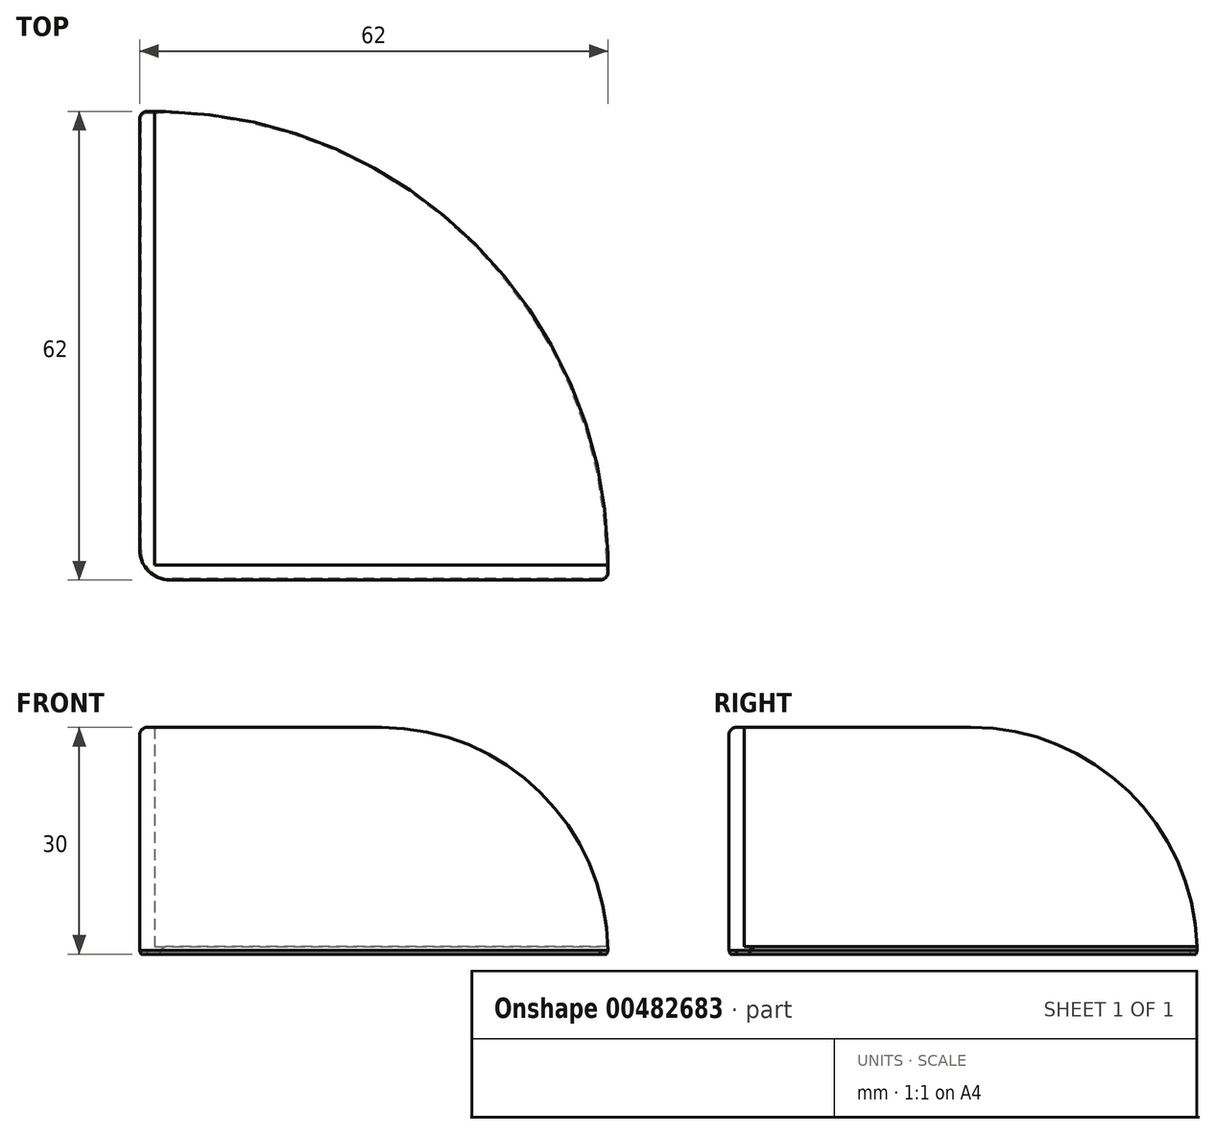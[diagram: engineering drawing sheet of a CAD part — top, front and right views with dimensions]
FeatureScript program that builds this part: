
annotation { "Feature Type Name" : "Feature", "Feature Type Description" : "" }
export const myFeature = defineFeature(function(context is Context, id is Id, definition is map)
    precondition{}
    {
        {
            var Q0;
            Q0=qCreatedBy(makeId("Top.planeOp"),FACE);
            var sketch = newSketch(context, id + "F0", { "sketchPlane" : qUnion([Q0])});
            skLineSegment(sketch, "E0.bottom", {"start": v(0, 0) * mm, "end": v(60, 0) * mm});
            skLineSegment(sketch, "E0.top", {"start": v(0, 60) * mm, "end": v(60, 60) * mm, "construction": true});
            skLineSegment(sketch, "E0.left", {"start": v(0, 0) * mm, "end": v(0, 60) * mm});
            skLineSegment(sketch, "E0.right", {"start": v(60, 0) * mm, "end": v(60, 60) * mm, "construction": true});
            skLineSegment(sketch, "E1", {"start": v(60, 0) * mm, "end": v(60, -2) * mm});
            skLineSegment(sketch, "E2", {"start": v(60, -2) * mm, "end": v(-2, -2) * mm});
            skLineSegment(sketch, "E3", {"start": v(-2, -2) * mm, "end": v(-2, 60) * mm});
            skLineSegment(sketch, "E4", {"start": v(-2, 60) * mm, "end": v(0, 60) * mm});
            skArc(sketch, "E5", {"start": v(60, 0) * mm, "mid": v(42.43, 42.43) * mm, "end": v(0, 60) * mm});
            skSolve(sketch);
        }
        {
            var Q0;
            Q0=makeQuery(id+"F0.imprint","IMPRINT",FACE,{"disambiguationData":[TD([[makeQuery(id+"F0.imprint","IMPRINT",EDGE,{"derivedFrom":sQuery(id+"F0.wireOp",EDGE,"E0.bottom")}),1.0]])]});
            extrude(context, id + "F1", {"entities" : qUnion([Q0]), "depth" : 1 * mm});
        }
        {
            var Q0;
            Q0=makeQuery(id+"F0.imprint","IMPRINT",FACE,{"disambiguationData":[TD([[makeQuery(id+"F0.imprint","IMPRINT",EDGE,{"derivedFrom":sQuery(id+"F0.wireOp",EDGE,"E0.bottom")}),-1.0]])]});
            extrude(context, id + "F2", {"entities" : qUnion([Q0]), "operationType" : NewBodyOperationType.ADD, "depth" : 30 * mm});
        }
        {
            var Q0;
            Q0=makeQuery(id+"F2.opExtrude","CAP_EDGE",EDGE,{"disambiguationData":[OSD([sQuery(id+"F0.wireOp",EDGE,"E1")])],"isStart":false});
            var Q1;
            Q1=makeQuery(id+"F2.opExtrude","CAP_EDGE",EDGE,{"disambiguationData":[OSD([sQuery(id+"F0.wireOp",EDGE,"E4")])],"isStart":false});
            fillet(context, id + "F3", {"entities" : qUnion([Q0, Q1]), "radius" : 30 * mm, "tangentPropagation" : true, "allowEdgeOverflow" : false});
        }
        {
            var Q0;
            Q0=makeQuery(id+"F2.opExtrude","SWEPT_EDGE",EDGE,{"disambiguationData":[OSD([sQuery(id+"F0.wireOp",EDGE,"E2"),sQuery(id+"F0.wireOp",EDGE,"E3")])]});
            fillet(context, id + "F4", {"entities" : qUnion([Q0]), "radius" : 4 * mm, "tangentPropagation" : true, "allowEdgeOverflow" : false});
        }
        {
            var Q0;
            Q0=makeQuery(id+"F3.opFillet","BLEND_EDGE",EDGE,{"blendedFrom":[makeQuery(id+"F2.opExtrude","CAP_EDGE",EDGE,{"disambiguationData":[OSD([sQuery(id+"F0.wireOp",EDGE,"E4")])],"isStart":false}),makeQuery(id+"F2.opExtrude","SWEPT_FACE",FACE,{"disambiguationData":[OSD([sQuery(id+"F0.wireOp",EDGE,"E3")])]})],"blendedInto":[makeQuery(id+"F2.opExtrude","SWEPT_FACE",FACE,{"disambiguationData":[OSD([sQuery(id+"F0.wireOp",EDGE,"E3")])]})]});
            var Q1;
            Q1=makeQuery(id+"F2.opExtrude","CAP_EDGE",EDGE,{"disambiguationData":[OSD([sQuery(id+"F0.wireOp",EDGE,"E3")])],"isStart":false});
            var Q2;
            Q2=makeQuery(id+"F3.opFillet","BLEND_EDGE",EDGE,{"blendedFrom":[makeQuery(id+"F2.opExtrude","CAP_EDGE",EDGE,{"disambiguationData":[OSD([sQuery(id+"F0.wireOp",EDGE,"E1")])],"isStart":false}),makeQuery(id+"F2.opExtrude","SWEPT_FACE",FACE,{"disambiguationData":[OSD([sQuery(id+"F0.wireOp",EDGE,"E2")])]})],"blendedInto":[makeQuery(id+"F2.opExtrude","SWEPT_FACE",FACE,{"disambiguationData":[OSD([sQuery(id+"F0.wireOp",EDGE,"E2")])]})]});
            var Q3;
            Q3=makeQuery(id+"F2.opExtrude","CAP_EDGE",EDGE,{"disambiguationData":[OSD([sQuery(id+"F0.wireOp",EDGE,"E2")])],"isStart":false});
            var Q4;
            {var subQ0=sQuery(id+"F0.wireOp",EDGE,"E3");var subQ1=sQuery(id+"F0.wireOp",EDGE,"E2");Q4=makeQuery(id+"F4.opFillet","BLEND_EDGE",EDGE,{"blendedFrom":[makeQuery(id+"F2.opExtrude","SWEPT_EDGE",EDGE,{"disambiguationData":[OSD([subQ1,subQ0])]}),makeQuery(id+"F2.opExtrude","CAP_FACE",FACE,{"disambiguationData":[OSD([sQuery(id+"F0.wireOp",EDGE,"E0.bottom"),sQuery(id+"F0.wireOp",EDGE,"E0.left"),sQuery(id+"F0.wireOp",EDGE,"E1"),subQ1,subQ0,sQuery(id+"F0.wireOp",EDGE,"E4")])],"isStart":false})],"blendedInto":[makeQuery(id+"F2.opExtrude","CAP_FACE",FACE,{"disambiguationData":[OSD([sQuery(id+"F0.wireOp",EDGE,"E0.bottom"),sQuery(id+"F0.wireOp",EDGE,"E0.left"),sQuery(id+"F0.wireOp",EDGE,"E1"),subQ1,subQ0,sQuery(id+"F0.wireOp",EDGE,"E4")])],"isStart":false})]});}
            var Q5;
            Q5=makeQuery(id+"F6.opChamfer","BLEND_EDGE",EDGE,{"blendedFrom":[makeQuery(id+"F1.opExtrude","CAP_EDGE",EDGE,{"disambiguationData":[OSD([sQuery(id+"F0.wireOp",EDGE,"E5")])],"isStart":true}),makeQuery(id+"F2.opExtrude","SWEPT_FACE",FACE,{"disambiguationData":[OSD([sQuery(id+"F0.wireOp",EDGE,"E2")])]})],"blendedInto":[makeQuery(id+"F2.opExtrude","SWEPT_FACE",FACE,{"disambiguationData":[OSD([sQuery(id+"F0.wireOp",EDGE,"E2")])]})]});
            var Q6;
            Q6=makeQuery(id+"F6.opChamfer","BLEND_EDGE",EDGE,{"blendedFrom":[makeQuery(id+"F1.opExtrude","CAP_EDGE",EDGE,{"disambiguationData":[OSD([sQuery(id+"F0.wireOp",EDGE,"E5")])],"isStart":true}),makeQuery(id+"F2.opExtrude","SWEPT_FACE",FACE,{"disambiguationData":[OSD([sQuery(id+"F0.wireOp",EDGE,"E3")])]})],"blendedInto":[makeQuery(id+"F2.opExtrude","SWEPT_FACE",FACE,{"disambiguationData":[OSD([sQuery(id+"F0.wireOp",EDGE,"E3")])]})]});
            fillet(context, id + "F5", {"entities" : qUnion([Q0, Q1, Q2, Q3, Q4, Q5, Q6]), "radius" : 1 * mm, "tangentPropagation" : true, "allowEdgeOverflow" : false});
        }
        {
            var Q0;
            Q0=makeQuery(id+"F1.opExtrude","CAP_EDGE",EDGE,{"disambiguationData":[OSD([sQuery(id+"F0.wireOp",EDGE,"E5")])],"isStart":true});
            var Q1;
            {var subQ0=sQuery(id+"F0.wireOp",EDGE,"E4");var subQ1=sQuery(id+"F0.wireOp",EDGE,"E0.left");var subQ2=sQuery(id+"F0.wireOp",EDGE,"E0.bottom");Q1=makeQuery(id+"F3.opFillet","BLEND_EDGE",EDGE,{"blendedFrom":[makeQuery(id+"F2.opExtrude","CAP_EDGE",EDGE,{"disambiguationData":[OSD([subQ0])],"isStart":false}),makeQuery(id+"F2.boolean.opBoolean","MERGE",FACE,{"derivedFrom":[makeQuery(id+"F1.opExtrude","CAP_FACE",FACE,{"disambiguationData":[OSD([subQ2,subQ1,sQuery(id+"F0.wireOp",EDGE,"E5")])],"isStart":true}),makeQuery(id+"F2.opExtrude","CAP_FACE",FACE,{"disambiguationData":[OSD([subQ2,subQ1,sQuery(id+"F0.wireOp",EDGE,"E1"),sQuery(id+"F0.wireOp",EDGE,"E2"),sQuery(id+"F0.wireOp",EDGE,"E3"),subQ0])],"isStart":true})]})],"blendedInto":[makeQuery(id+"F2.boolean.opBoolean","MERGE",FACE,{"derivedFrom":[makeQuery(id+"F1.opExtrude","CAP_FACE",FACE,{"disambiguationData":[OSD([subQ2,subQ1,sQuery(id+"F0.wireOp",EDGE,"E5")])],"isStart":true}),makeQuery(id+"F2.opExtrude","CAP_FACE",FACE,{"disambiguationData":[OSD([subQ2,subQ1,sQuery(id+"F0.wireOp",EDGE,"E1"),sQuery(id+"F0.wireOp",EDGE,"E2"),sQuery(id+"F0.wireOp",EDGE,"E3"),subQ0])],"isStart":true})]})]});}
            var Q2;
            Q2=makeQuery(id+"F2.opExtrude","CAP_EDGE",EDGE,{"disambiguationData":[OSD([sQuery(id+"F0.wireOp",EDGE,"E3")])],"isStart":true});
            var Q3;
            {var subQ0=sQuery(id+"F0.wireOp",EDGE,"E3");var subQ1=sQuery(id+"F0.wireOp",EDGE,"E2");var subQ2=sQuery(id+"F0.wireOp",EDGE,"E0.left");var subQ3=sQuery(id+"F0.wireOp",EDGE,"E0.bottom");Q3=makeQuery(id+"F4.opFillet","BLEND_EDGE",EDGE,{"blendedFrom":[makeQuery(id+"F2.opExtrude","SWEPT_EDGE",EDGE,{"disambiguationData":[OSD([subQ1,subQ0])]}),makeQuery(id+"F2.boolean.opBoolean","MERGE",FACE,{"derivedFrom":[makeQuery(id+"F1.opExtrude","CAP_FACE",FACE,{"disambiguationData":[OSD([subQ3,subQ2,sQuery(id+"F0.wireOp",EDGE,"E5")])],"isStart":true}),makeQuery(id+"F2.opExtrude","CAP_FACE",FACE,{"disambiguationData":[OSD([subQ3,subQ2,sQuery(id+"F0.wireOp",EDGE,"E1"),subQ1,subQ0,sQuery(id+"F0.wireOp",EDGE,"E4")])],"isStart":true})]})],"blendedInto":[makeQuery(id+"F2.boolean.opBoolean","MERGE",FACE,{"derivedFrom":[makeQuery(id+"F1.opExtrude","CAP_FACE",FACE,{"disambiguationData":[OSD([subQ3,subQ2,sQuery(id+"F0.wireOp",EDGE,"E5")])],"isStart":true}),makeQuery(id+"F2.opExtrude","CAP_FACE",FACE,{"disambiguationData":[OSD([subQ3,subQ2,sQuery(id+"F0.wireOp",EDGE,"E1"),subQ1,subQ0,sQuery(id+"F0.wireOp",EDGE,"E4")])],"isStart":true})]})]});}
            var Q4;
            Q4=makeQuery(id+"F2.opExtrude","CAP_EDGE",EDGE,{"disambiguationData":[OSD([sQuery(id+"F0.wireOp",EDGE,"E2")])],"isStart":true});
            var Q5;
            {var subQ0=sQuery(id+"F0.wireOp",EDGE,"E1");var subQ1=sQuery(id+"F0.wireOp",EDGE,"E0.left");var subQ2=sQuery(id+"F0.wireOp",EDGE,"E0.bottom");Q5=makeQuery(id+"F3.opFillet","BLEND_EDGE",EDGE,{"blendedFrom":[makeQuery(id+"F2.opExtrude","CAP_EDGE",EDGE,{"disambiguationData":[OSD([subQ0])],"isStart":false}),makeQuery(id+"F2.boolean.opBoolean","MERGE",FACE,{"derivedFrom":[makeQuery(id+"F1.opExtrude","CAP_FACE",FACE,{"disambiguationData":[OSD([subQ2,subQ1,sQuery(id+"F0.wireOp",EDGE,"E5")])],"isStart":true}),makeQuery(id+"F2.opExtrude","CAP_FACE",FACE,{"disambiguationData":[OSD([subQ2,subQ1,subQ0,sQuery(id+"F0.wireOp",EDGE,"E2"),sQuery(id+"F0.wireOp",EDGE,"E3"),sQuery(id+"F0.wireOp",EDGE,"E4")])],"isStart":true})]})],"blendedInto":[makeQuery(id+"F2.boolean.opBoolean","MERGE",FACE,{"derivedFrom":[makeQuery(id+"F1.opExtrude","CAP_FACE",FACE,{"disambiguationData":[OSD([subQ2,subQ1,sQuery(id+"F0.wireOp",EDGE,"E5")])],"isStart":true}),makeQuery(id+"F2.opExtrude","CAP_FACE",FACE,{"disambiguationData":[OSD([subQ2,subQ1,subQ0,sQuery(id+"F0.wireOp",EDGE,"E2"),sQuery(id+"F0.wireOp",EDGE,"E3"),sQuery(id+"F0.wireOp",EDGE,"E4")])],"isStart":true})]})]});}
            chamfer(context, id + "F6", {"entities" : qUnion([Q0, Q1, Q2, Q3, Q4, Q5]), "chamferType" : ChamferType.OFFSET_ANGLE, "width" : 0.5 * mm, "oppositeDirection" : false, "angle" : 20 * degree, "tangentPropagation" : true});
        }
    });
